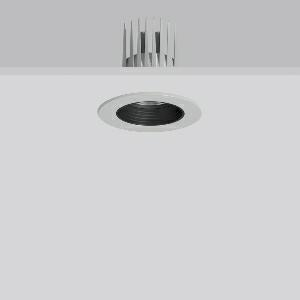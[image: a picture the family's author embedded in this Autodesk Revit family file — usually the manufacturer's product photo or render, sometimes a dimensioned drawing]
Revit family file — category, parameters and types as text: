
# Revit family: heledon_mini_e_901746_004_b9da
name_source: partatom
category: Lighting Fixtures
units: mm (PartAtom-declared; Revit-internal decimal feet)

## family parameters
Cut with Voids When Loaded = No
Host = Face
Light Source = No
Part Type = Normal
Room Calculation Point = No
Round Connector Dimension = Use Diameter
Shared = No

## types (1)
- HELEDON mini E (1 x LED Modul 930, 2250 lm, 3000)
    Apparent Load = 20 VA
    Approval mark = CE
    CIE Flux Codes = 80 99 100 100 100
    Color Rendering = 90
    Color Temperature = 3000
    Default Elevation = 1800 mm
    Description = Series: HELEDON mini
Round recessed downlight. Housing: die-cast aluminium, powder-coated. Black plastic ring and recessed LED to prevent glare from the side. Optical assembly with lens made of plastic (polycarbonate) for the best homogeneous light distribution - can be changed without tools. Best colour rendering index Ra>90. Suitable for Recessed ceiling mounting. Installation without tools thanks to spring fastening system. Including separate LED converter with connecting cable 600 mm.High quality converter without flickering and stroboscopic effect. Through-wiring box (5 pole) available as accessory. The following accessories can be mounted without use of tools: interchangeable lenses, decorative glasses, honeycomb louvre, clear and frosted diffusers, white interchangeable plastic ring. 
Colour: silver
Diameter: 124 mm
Height: 3 mm
Cut-out diameter: 114 mm
Recess height: 170 mm
Luminaire: recess height: 120 mm
Lamp: LED
Socket: without socket
Colour temperature: 3000K
Colour rendering index (CRI): 92
System power: 20 W
Rated luminous flux: 2250 lm
Luminous efficiency: 113 lm/W
Control gear: Regulated power supply
Protection class: II
Type of protection: IP 20
    Height = 0 mm  [stored 0 ft]
    Lamp = 1 x LED Modul 930
    Lamp Light Flux = 2250 lm
    Lamp count = 1
    Length = 124 mm  [stored 0.406824 ft]
    Lifetime = 50000 h
    Luminous efficacy = 113 lm/W
    Manufacturer = RZB
    ModVariant = No
    Model = 901746.004
    Mounting Place = Ceiling
    Mounting Type = Recessed
    Number of Poles = 1
    OnlyDefault = Yes
    Power Factor = 1
    Product Name = HELEDON mini E
    Product group = Recessed downlights
    ProductGroupID = 402
    Protection Class = Protection class II
    Protection Degree = IP 20
    RLX_Detail_Level = 1
    RLX_Emergency_Light_Flux = 0 lm
    RLX_Emergency_Type = 0
    RLX_Emergency_Type_DB = No
    RlxData = <blob elided: 124649 chars, md5=e035e350>
    Socket = socket
    Standby Power = 0 W
    System Light Flux = 2250 lm
    System Power = 20 W
    Type Comments = Product without accessories
    Type Image = 901656.004.jpg
    URL = http://relux.com
    VarID = ---
    Voltage = 230 V
    Voltage Range = 220-240 V
    Weight = 0.00 kg
    Width = 0 mm  [stored 0 ft]

note: [stored X ft] marks values corroborated as IEEE doubles in the binary element streams (Revit-internal decimal feet)

## geometry (parser evidence)
native form markers: Blend x4, Sweep x10
no freeform markers — native parametric forms only
